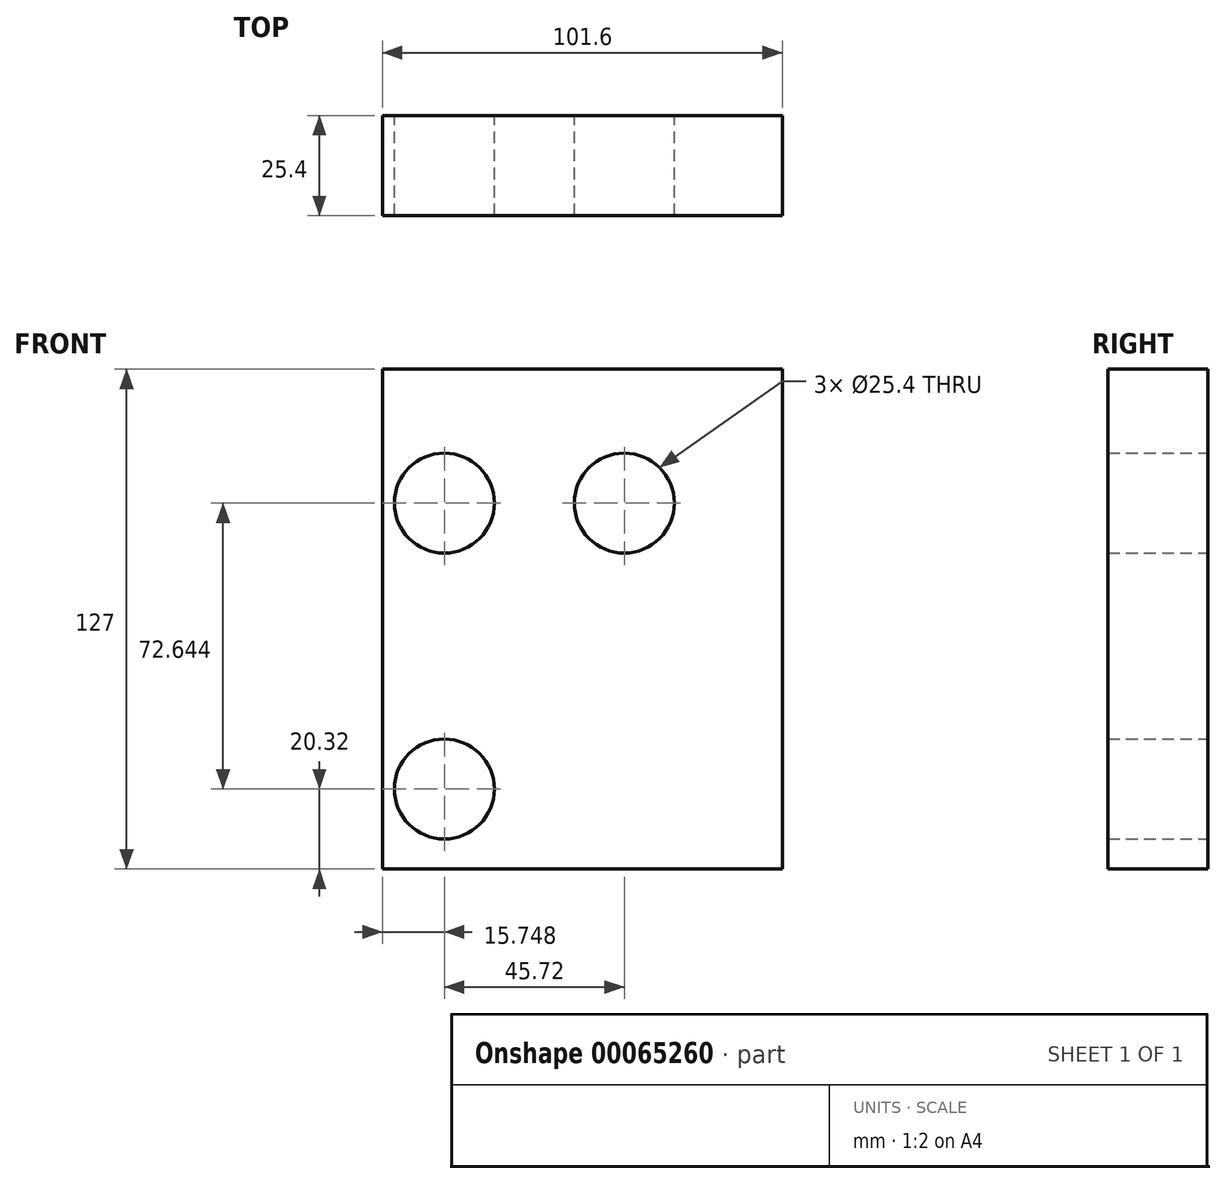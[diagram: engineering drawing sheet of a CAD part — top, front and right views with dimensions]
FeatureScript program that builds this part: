
annotation { "Feature Type Name" : "Feature", "Feature Type Description" : "" }
export const myFeature = defineFeature(function(context is Context, id is Id, definition is map)
    precondition{}
    {
        {
            var Q0;
            Q0=qCreatedBy(makeId("Front.planeOp"),FACE);
            var sketch = newSketch(context, id + "F0", { "sketchPlane" : qUnion([Q0])});
            skLineSegment(sketch, "E0.rect.bottom", {"start": v(-50.8, 63.5) * mm, "end": v(50.8, 63.5) * mm});
            skLineSegment(sketch, "E0.rect.top", {"start": v(-50.8, -63.5) * mm, "end": v(50.8, -63.5) * mm});
            skLineSegment(sketch, "E0.rect.left", {"start": v(-50.8, 63.5) * mm, "end": v(-50.8, -63.5) * mm});
            skLineSegment(sketch, "E0.rect.right", {"start": v(50.8, 63.5) * mm, "end": v(50.8, -63.5) * mm});
            skPoint(sketch, "E0.rect.middle", {"position": v(0, 0) * mm});
            skLineSegment(sketch, "E1.bottom", {"start": v(50.8, -63.5) * mm, "end": v(0, -63.5) * mm});
            skLineSegment(sketch, "E1.left", {"start": v(50.8, -63.5) * mm, "end": v(50.8, -12.7) * mm});
            skCircle(sketch, "E2", {"center": v(-35.05, -43.18) * mm, "radius": 12.7 * mm});
            skCircle(sketch, "E3", {"center": v(-35.05, 29.46) * mm, "radius": 12.7 * mm});
            skCircle(sketch, "E4", {"center": v(10.67, 29.46) * mm, "radius": 12.7 * mm});
            skLineSegment(sketch, "E5", {"start": v(-35.05, 29.46) * mm, "end": v(10.67, 29.46) * mm});
            skLineSegment(sketch, "E6", {"start": v(-35.05, 29.46) * mm, "end": v(-35.05, -43.18) * mm});
            skLineSegment(sketch, "E7", {"start": v(-35.05, -43.18) * mm, "end": v(-35.05, -63.5) * mm});
            skLineSegment(sketch, "E8", {"start": v(-50.8, -63.5) * mm, "end": v(-35.05, -63.5) * mm});
            skLineSegment(sketch, "E9", {"start": v(-35.05, -63.5) * mm, "end": v(-50.8, -63.5) * mm});
            skLineSegment(sketch, "E10", {"start": v(-35.05, -43.18) * mm, "end": v(-50.8, -43.18) * mm});
            skSolve(sketch);
        }
        {
            var Q0;
            Q0 = qSketchRegion(id + "F0", true);
            extrude(context, id + "F1", {"entities" : qUnion([Q0]), "depth" : 25.4 * mm});
        }
    });
